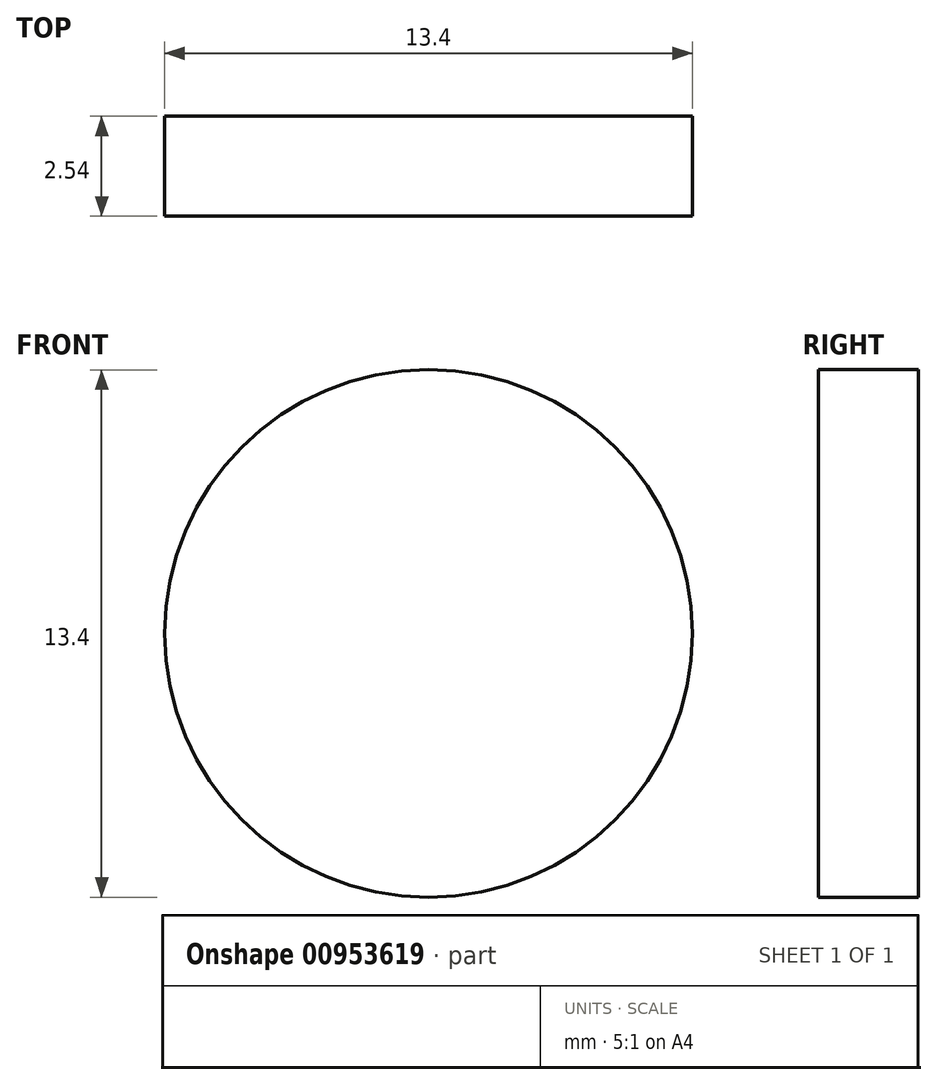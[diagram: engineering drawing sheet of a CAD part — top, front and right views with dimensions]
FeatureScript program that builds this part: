
annotation { "Feature Type Name" : "Feature", "Feature Type Description" : "" }
export const myFeature = defineFeature(function(context is Context, id is Id, definition is map)
    precondition{}
    {
        {
            var Q0;
            Q0=qCreatedBy(makeId("Front.planeOp"),FACE);
            var sketch = newSketch(context, id + "F0", { "sketchPlane" : qUnion([Q0])});
            skCircle(sketch, "E0", {"center": v(0, 0) * mm, "radius": 6.7 * mm});
            skSolve(sketch);
        }
        {
            var Q0;
            Q0 = qSketchRegion(id + "F0", true);
            extrude(context, id + "F1", {"entities" : qUnion([Q0]), "depth" : 2.54 * mm, "offsetDistance" : 25.4 * mm});
        }
    });
